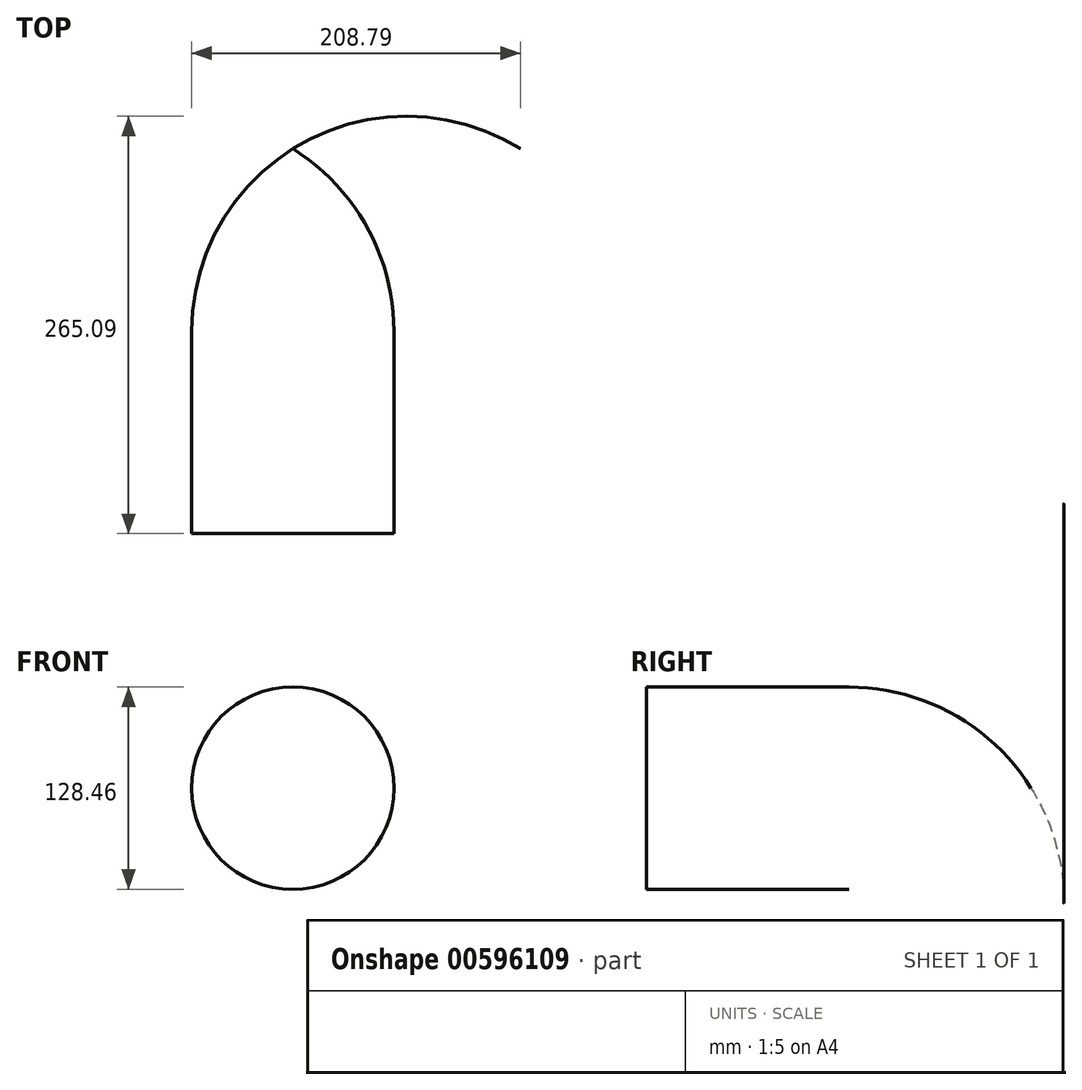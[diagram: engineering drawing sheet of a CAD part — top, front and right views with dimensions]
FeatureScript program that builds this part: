
annotation { "Feature Type Name" : "Feature", "Feature Type Description" : "" }
export const myFeature = defineFeature(function(context is Context, id is Id, definition is map)
    precondition{}
    {
        {
            var Q0;
            Q0=qCreatedBy(makeId("Top.planeOp"),FACE);
            var sketch = newSketch(context, id + "F0", { "sketchPlane" : qUnion([Q0])});
            skLineSegment(sketch, "E0.bottom", {"start": v(-34.09, -29.56) * mm, "end": v(30.15, -29.56) * mm});
            skLineSegment(sketch, "E0.left", {"start": v(-34.09, -29.56) * mm, "end": v(-34.09, 99.02) * mm});
            skLineSegment(sketch, "E0.right", {"start": v(30.15, -29.56) * mm, "end": v(30.15, 99.02) * mm});
            skLineSegment(sketch, "E1", {"start": v(-34.09, 99.02) * mm, "end": v(-34.09, 214.83) * mm});
            skArc(sketch, "E2", {"start": v(30.15, 99.02) * mm, "mid": v(13.01, 165.24) * mm, "end": v(-34.09, 214.83) * mm});
            skSolve(sketch);
        }
        {
            var Q0;
            Q0=makeQuery(id+"F0.imprint","IMPRINT",FACE,{"disambiguationData":[TD([[makeQuery(id+"F0.imprint","IMPRINT",EDGE,{"derivedFrom":sQuery(id+"F0.wireOp",EDGE,"E0.bottom")}),1.0]])]});
            var Q1;
            Q1=sQuery(id+"F0.wireOp",EDGE,"E0.left");
            revolve(context, id + "F1", {"entities" : qUnion([Q0]), "axis" : qUnion([Q1]), "revolveType" : RevolveType.FULL});
        }
    });
